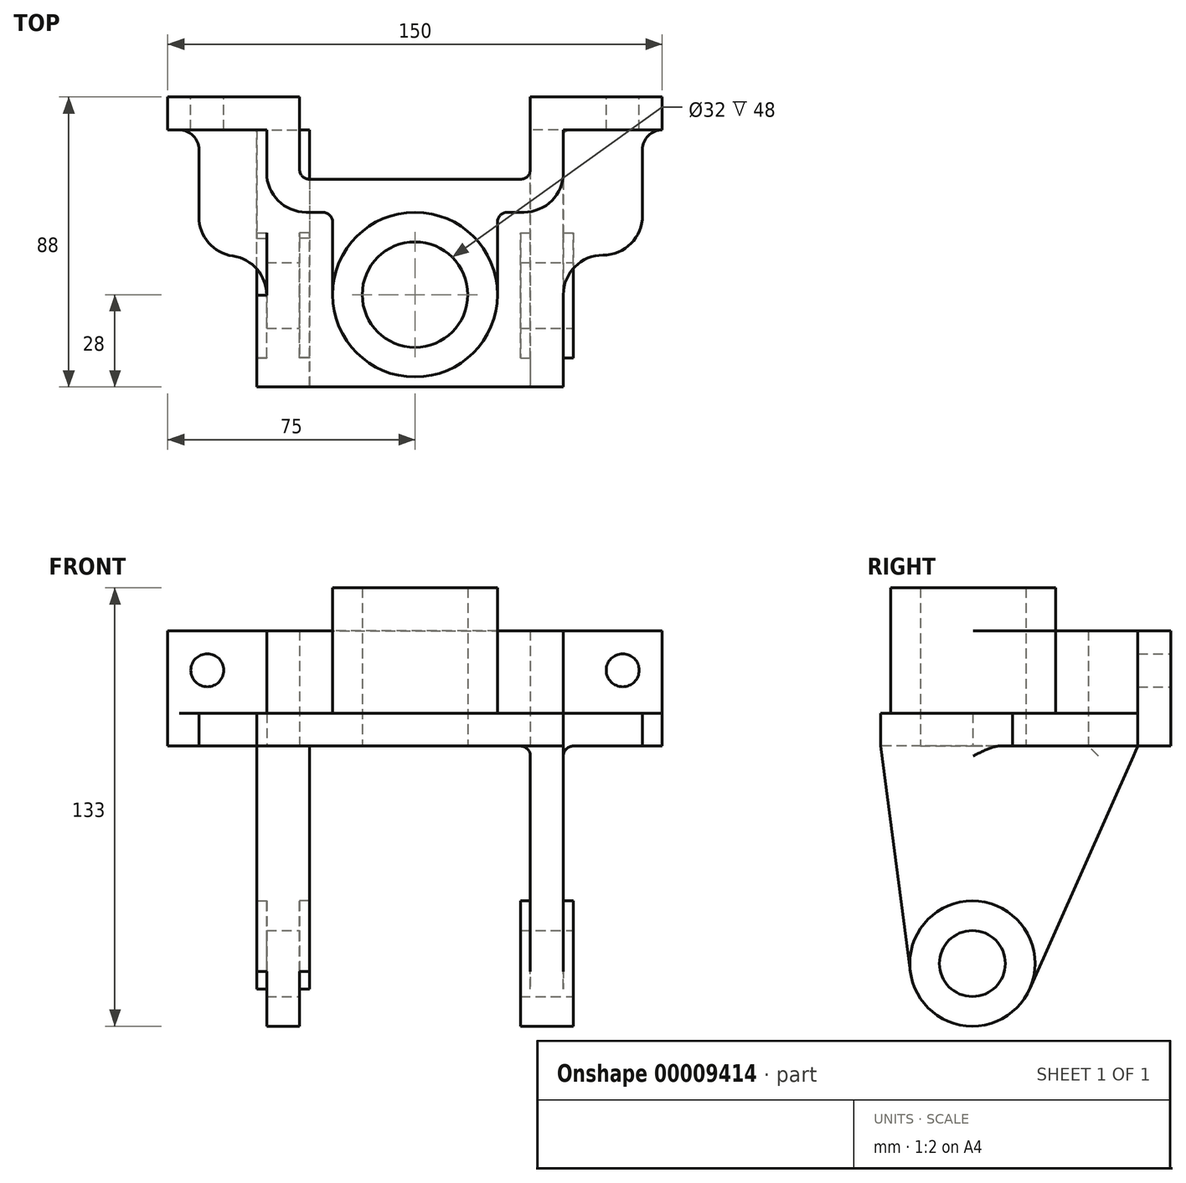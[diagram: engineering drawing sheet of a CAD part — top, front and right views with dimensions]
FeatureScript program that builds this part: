
annotation { "Feature Type Name" : "Feature", "Feature Type Description" : "" }
export const myFeature = defineFeature(function(context is Context, id is Id, definition is map)
    precondition{}
    {
        {
            var Q0;
            Q0=qCreatedBy(makeId("Top.planeOp"),FACE);
            var sketch = newSketch(context, id + "F0", { "sketchPlane" : qUnion([Q0])});
            skLineSegment(sketch, "E0", {"start": v(0, 35) * mm, "end": v(-32, 35) * mm});
            skLineSegment(sketch, "E1", {"start": v(-35, 38) * mm, "end": v(-35, 60) * mm});
            skLineSegment(sketch, "E2", {"start": v(-35, 60) * mm, "end": v(-75, 60) * mm});
            skLineSegment(sketch, "E3", {"start": v(-75, 60) * mm, "end": v(-75, 50) * mm});
            skLineSegment(sketch, "E4", {"start": v(-75, 50) * mm, "end": v(-71.53, 50) * mm});
            skLineSegment(sketch, "E5", {"start": v(-45, 50) * mm, "end": v(-45, 37) * mm});
            skLineSegment(sketch, "E6", {"start": v(-33, 25) * mm, "end": v(-28, 25) * mm});
            skLineSegment(sketch, "E7.0.MirrorCS", {"start": v(35, 38) * mm, "end": v(35, 60) * mm});
            skLineSegment(sketch, "E7.1.MirrorCS", {"start": v(0, 35) * mm, "end": v(32, 35) * mm});
            skLineSegment(sketch, "E7.2.MirrorCS", {"start": v(75, 60) * mm, "end": v(75, 50) * mm});
            skLineSegment(sketch, "E7.3.MirrorCS", {"start": v(33, 25) * mm, "end": v(28, 25) * mm});
            skLineSegment(sketch, "E7.4.MirrorCS", {"start": v(35, 60) * mm, "end": v(75, 60) * mm});
            skLineSegment(sketch, "E7.5.MirrorCS", {"start": v(75, 50) * mm, "end": v(75, 50) * mm});
            skLineSegment(sketch, "E7.6.MirrorCS", {"start": v(45, 50) * mm, "end": v(45, 37) * mm});
            skPoint(sketch, "E8.visualSharp", {"position": v(-35, 35) * mm});
            skArc(sketch, "E8.filletArc", {"start": v(-35, 38) * mm, "mid": v(-34.12, 35.88) * mm, "end": v(-32, 35) * mm});
            skPoint(sketch, "E9.visualSharp", {"position": v(35, 35) * mm});
            skArc(sketch, "E9.filletArc", {"start": v(32, 35) * mm, "mid": v(34.12, 35.88) * mm, "end": v(35, 38) * mm});
            skPoint(sketch, "E10.visualSharp", {"position": v(-45, 25) * mm});
            skArc(sketch, "E10.filletArc", {"start": v(-45, 37) * mm, "mid": v(-41.49, 28.51) * mm, "end": v(-33, 25) * mm});
            skArc(sketch, "E11.filletArc", {"start": v(33, 25) * mm, "mid": v(41.49, 28.51) * mm, "end": v(45, 37) * mm});
            skLineSegment(sketch, "E12", {"start": v(-65.53, 44) * mm, "end": v(-65.53, 23.6) * mm});
            skLineSegment(sketch, "E13", {"start": v(-45, -0.16) * mm, "end": v(-45, -28) * mm});
            skLineSegment(sketch, "E14", {"start": v(-45, -28) * mm, "end": v(45, -28) * mm});
            skLineSegment(sketch, "E15", {"start": v(45, -28) * mm, "end": v(45, 0) * mm});
            skLineSegment(sketch, "E16", {"start": v(69, 24) * mm, "end": v(69, 44) * mm});
            skPoint(sketch, "E17.newPointA", {"position": v(-45, 50) * mm});
            skArc(sketch, "E17.filletArc", {"start": v(-65.53, 44) * mm, "mid": v(-67.29, 48.24) * mm, "end": v(-71.53, 50) * mm});
            skLineSegment(sketch, "E18", {"start": v(-71.53, 50) * mm, "end": v(-45, 50) * mm});
            skPoint(sketch, "E19.newPointA", {"position": v(45, 50) * mm});
            skArc(sketch, "E19.filletArc", {"start": v(75, 50) * mm, "mid": v(70.76, 48.24) * mm, "end": v(69, 44) * mm});
            skLineSegment(sketch, "E20", {"start": v(45, 50) * mm, "end": v(75, 50) * mm});
            skPoint(sketch, "E21.visualSharp", {"position": v(-65.53, 12.1) * mm});
            skArc(sketch, "E21.filletArc", {"start": v(-65.53, 23.6) * mm, "mid": v(-62.6, 15.74) * mm, "end": v(-55.27, 11.72) * mm});
            skPoint(sketch, "E22.visualSharp", {"position": v(69, 11.84) * mm});
            skArc(sketch, "E22.filletArc", {"start": v(57, 12) * mm, "mid": v(65.49, 15.51) * mm, "end": v(69, 24) * mm});
            skCircle(sketch, "E23", {"center": v(0, 0) * mm, "radius": 25 * mm});
            skCircle(sketch, "E24", {"center": v(0, 0) * mm, "radius": 16 * mm});
            skLineSegment(sketch, "E25", {"start": v(25, 0) * mm, "end": v(25, 22) * mm});
            skLineSegment(sketch, "E26", {"start": v(-25, 0) * mm, "end": v(-25, 22) * mm});
            skPoint(sketch, "E27.orphan", {"position": v(0, 25) * mm});
            skPoint(sketch, "E28.visualSharp", {"position": v(-25, 25) * mm});
            skArc(sketch, "E28.filletArc", {"start": v(-25, 22) * mm, "mid": v(-25.88, 24.12) * mm, "end": v(-28, 25) * mm});
            skPoint(sketch, "E29.visualSharp", {"position": v(25, 25) * mm});
            skArc(sketch, "E29.filletArc", {"start": v(28, 25) * mm, "mid": v(25.88, 24.12) * mm, "end": v(25, 22) * mm});
            skPoint(sketch, "E30.visualSharp", {"position": v(45, 11.84) * mm});
            skArc(sketch, "E30.filletArc", {"start": v(57, 12) * mm, "mid": v(48.51, 8.49) * mm, "end": v(45, 0) * mm});
            skPoint(sketch, "E31.visualSharp", {"position": v(-45, 11.84) * mm});
            skArc(sketch, "E31.filletArc", {"start": v(-45, -0.16) * mm, "mid": v(-47.92, 7.7) * mm, "end": v(-55.27, 11.72) * mm});
            skLineSegment(sketch, "E32", {"start": v(-35, -0.16) * mm, "end": v(-35, -28) * mm});
            skLineSegment(sketch, "E33", {"start": v(35, 25.17) * mm, "end": v(35, -28) * mm});
            skLineSegment(sketch, "E34", {"start": v(45, 0) * mm, "end": v(45, 25) * mm});
            skLineSegment(sketch, "E35", {"start": v(-35, -0.16) * mm, "end": v(-35, 25.17) * mm});
            skLineSegment(sketch, "E36", {"start": v(-45, -0.16) * mm, "end": v(-45, 25) * mm});
            skLineSegment(sketch, "E37", {"start": v(45, 25) * mm, "end": v(45, 37) * mm});
            skLineSegment(sketch, "E38", {"start": v(-45, 25) * mm, "end": v(-45, 37) * mm});
            skLineSegment(sketch, "E39", {"start": v(45, 50) * mm, "end": v(35, 50) * mm});
            skLineSegment(sketch, "E40", {"start": v(35, 25.17) * mm, "end": v(35, 38) * mm});
            skLineSegment(sketch, "E41", {"start": v(-35, 25.17) * mm, "end": v(-35, 38) * mm});
            skLineSegment(sketch, "E42", {"start": v(-45, 50) * mm, "end": v(-35, 50) * mm});
            skSolve(sketch);
        }
        {
            var Q0;
            Q0=makeQuery(id+"F0.imprint","IMPRINT",FACE,{"disambiguationData":[TD([[makeQuery(id+"F0.imprint","IMPRINT",EDGE,{"derivedFrom":sQuery(id+"F0.wireOp",EDGE,"E24")}),-1.0]])]});
            extrude(context, id + "F1", {"entities" : qUnion([Q0]), "depth" : 48 * mm});
        }
        {
            var Q0;
            Q0=makeQuery(id+"F0.imprint","IMPRINT",FACE,{"disambiguationData":[TD([[makeQuery(id+"F0.imprint","IMPRINT",EDGE,{"derivedFrom":sQuery(id+"F0.wireOp",EDGE,"E0")}),1.0]])]});
            var Q1;
            Q1=makeQuery(id+"F0.imprint","IMPRINT",FACE,{"disambiguationData":[TD([[makeQuery(id+"F0.imprint","IMPRINT",EDGE,{"derivedFrom":sQuery(id+"F0.wireOp",EDGE,"E7.2.MirrorCS")}),-1.0]])]});
            var Q2;
            {var subQ3=sQuery(id+"F0.wireOp",EDGE,"E7.6.MirrorCS");Q2=makeQuery(id+"F0.imprint","IMPRINT",FACE,{"disambiguationData":[TD([[makeQuery(id+"F0.imprint","IMPRINT",EDGE,{"derivedFrom":subQ3}),-1.0]])]});}
            var Q3;
            {var subQ3=sQuery(id+"F0.wireOp",EDGE,"E5");Q3=makeQuery(id+"F0.imprint","IMPRINT",FACE,{"disambiguationData":[TD([[makeQuery(id+"F0.imprint","IMPRINT",EDGE,{"derivedFrom":subQ3}),1.0]])]});}
            var Q4;
            {var subQ1=sQuery(id+"F0.wireOp",EDGE,"E2");Q4=makeQuery(id+"F0.imprint","IMPRINT",FACE,{"disambiguationData":[TD([[makeQuery(id+"F0.imprint","IMPRINT",EDGE,{"derivedFrom":subQ1}),1.0]])]});}
            extrude(context, id + "F2", {"entities" : qUnion([Q0, Q1, Q2, Q3, Q4]), "operationType" : NewBodyOperationType.ADD, "depth" : 35 * mm});
        }
        {
            var Q0;
            Q0=makeQuery(id+"F0.imprint","IMPRINT",FACE,{"disambiguationData":[TD([[makeQuery(id+"F0.imprint","IMPRINT",EDGE,{"derivedFrom":sQuery(id+"F0.wireOp",EDGE,"E5")}),-1.0]])]});
            var Q1;
            {var subQ2=sQuery(id+"F0.wireOp",EDGE,"E13");Q1=makeQuery(id+"F0.imprint","IMPRINT",FACE,{"disambiguationData":[TD([[makeQuery(id+"F0.imprint","IMPRINT",EDGE,{"derivedFrom":subQ2}),1.0]])]});}
            var Q2;
            {var subQ1=sQuery(id+"F0.wireOp",EDGE,"E15");Q2=makeQuery(id+"F0.imprint","IMPRINT",FACE,{"disambiguationData":[TD([[makeQuery(id+"F0.imprint","IMPRINT",EDGE,{"derivedFrom":subQ1}),1.0]])]});}
            var Q3;
            {var subQ2=sQuery(id+"F0.wireOp",EDGE,"E7.6.MirrorCS");Q3=makeQuery(id+"F0.imprint","IMPRINT",FACE,{"disambiguationData":[TD([[makeQuery(id+"F0.imprint","IMPRINT",EDGE,{"derivedFrom":subQ2}),1.0]])]});}
            var Q4;
            {var subQ8=sQuery(id+"F0.wireOp",EDGE,"E6");Q4=makeQuery(id+"F0.imprint","IMPRINT",FACE,{"disambiguationData":[TD([[makeQuery(id+"F0.imprint","IMPRINT",EDGE,{"derivedFrom":subQ8}),-1.0]])]});}
            var Q5;
            {var subQ1=sQuery(id+"F0.wireOp",EDGE,"d0786e6e-3a46-4e64-bf30-19189b01eaf3");Q5=makeQuery(id+"F0.imprint","IMPRINT",FACE,{"disambiguationData":[TD([[makeQuery(id+"F0.imprint","IMPRINT",EDGE,{"derivedFrom":subQ1}),-1.0]])]});}
            var Q6;
            {var subQ1=sQuery(id+"F0.wireOp",EDGE,"a1b5c434-1ed9-493c-be9e-ea0c3d859ba8");Q6=makeQuery(id+"F0.imprint","IMPRINT",FACE,{"disambiguationData":[TD([[makeQuery(id+"F0.imprint","IMPRINT",EDGE,{"derivedFrom":subQ1}),1.0]])]});}
            extrude(context, id + "F3", {"entities" : qUnion([Q0, Q1, Q2, Q3, Q4, Q5, Q6]), "operationType" : NewBodyOperationType.ADD, "depth" : 10 * mm});
        }
        {
            var Q0;
            Q0=makeQuery(id+"F2.opExtrude","SWEPT_FACE",FACE,{"disambiguationData":[OSD([sQuery(id+"F0.wireOp",EDGE,"E7.4.MirrorCS")])]});
            var sketch = newSketch(context, id + "F4", { "sketchPlane" : qUnion([Q0])});
            skCircle(sketch, "E43", {"center": v(-63, 23) * mm, "radius": 5 * mm});
            skCircle(sketch, "E44", {"center": v(63, 23) * mm, "radius": 5 * mm});
            skSolve(sketch);
        }
        {
            var Q0;
            Q0=makeQuery(id+"F4.imprint","IMPRINT",FACE,{"disambiguationData":[TD([[makeQuery(id+"F4.imprint","IMPRINT",EDGE,{"derivedFrom":sQuery(id+"F4.wireOp",EDGE,"E43")}),1.0]])]});
            var Q1;
            Q1=makeQuery(id+"F4.imprint","IMPRINT",FACE,{"disambiguationData":[TD([[makeQuery(id+"F4.imprint","IMPRINT",EDGE,{"derivedFrom":sQuery(id+"F4.wireOp",EDGE,"E44")}),1.0]])]});
            var Q2;
            Q2=makeQuery(id+"F2.opExtrude","SWEPT_FACE",FACE,{"disambiguationData":[OSD([sQuery(id+"F0.wireOp",EDGE,"E4"),sQuery(id+"F0.wireOp",EDGE,"E18")])]});
            extrude(context, id + "F5", {"entities" : qUnion([Q0, Q1]), "operationType" : NewBodyOperationType.REMOVE, "endBound" : BoundingType.UP_TO_SURFACE, "oppositeDirection" : true, "endBoundEntityFace" : qUnion([Q2]), "depth" : 25 * mm});
        }
        {
            var Q0;
            {var subQ2=sQuery(id+"F0.wireOp",EDGE,"E13");Q0=makeQuery(id+"F0.imprint","IMPRINT",FACE,{"disambiguationData":[TD([[makeQuery(id+"F0.imprint","IMPRINT",EDGE,{"derivedFrom":subQ2}),1.0]])]});}
            var Q1;
            {var subQ1=sQuery(id+"F0.wireOp",EDGE,"E15");Q1=makeQuery(id+"F0.imprint","IMPRINT",FACE,{"disambiguationData":[TD([[makeQuery(id+"F0.imprint","IMPRINT",EDGE,{"derivedFrom":subQ1}),1.0]])]});}
            var Q2;
            {var subQ3=sQuery(id+"F0.wireOp",EDGE,"E5");Q2=makeQuery(id+"F0.imprint","IMPRINT",FACE,{"disambiguationData":[TD([[makeQuery(id+"F0.imprint","IMPRINT",EDGE,{"derivedFrom":subQ3}),1.0]])]});}
            var Q3;
            {var subQ3=sQuery(id+"F0.wireOp",EDGE,"E7.6.MirrorCS");Q3=makeQuery(id+"F0.imprint","IMPRINT",FACE,{"disambiguationData":[TD([[makeQuery(id+"F0.imprint","IMPRINT",EDGE,{"derivedFrom":subQ3}),-1.0]])]});}
            extrude(context, id + "F6", {"entities" : qUnion([Q0, Q1, Q2, Q3]), "operationType" : NewBodyOperationType.ADD, "oppositeDirection" : true, "depth" : 100 * mm});
        }
        {
            var Q0;
            {var subQ0=sQuery(id+"F0.wireOp",EDGE,"E15");Q0=makeQuery(id+"F6.boolean.opBoolean","MERGE",FACE,{"derivedFrom":[makeQuery(id+"F3.opExtrude","SWEPT_FACE",FACE,{"disambiguationData":[OSD([subQ0])]}),makeQuery(id+"F6.opExtrude","SWEPT_FACE",FACE,{"disambiguationData":[OSD([subQ0,sQuery(id+"F0.wireOp",EDGE,"E34")])]})]});}
            var sketch = newSketch(context, id + "F7", { "sketchPlane" : qUnion([Q0])});
            skCircle(sketch, "E45", {"center": v(-0.22, -66) * mm, "radius": 10 * mm});
            skArc(sketch, "E46", {"start": v(-19.06, -68.46) * mm, "mid": v(-2.95, -84.8) * mm, "end": v(17.14, -73.73) * mm});
            skLineSegment(sketch, "E47", {"start": v(-28, 0) * mm, "end": v(-19.06, -68.46) * mm});
            skLineSegment(sketch, "E48", {"start": v(-28, 0) * mm, "end": v(50, 0) * mm});
            skLineSegment(sketch, "E49", {"start": v(50, 0) * mm, "end": v(17.14, -73.73) * mm});
            skLineSegment(sketch, "E50", {"start": v(50, 0) * mm, "end": v(-28, 0) * mm});
            skArc(sketch, "E51", {"start": v(17.14, -73.73) * mm, "mid": v(2.52, -47.2) * mm, "end": v(-19.06, -68.46) * mm});
            skSolve(sketch);
        }
        {
            var Q0;
            Q0=makeQuery(id+"F7.imprint","IMPRINT",FACE,{"disambiguationData":[TD([[makeQuery(id+"F7.imprint","IMPRINT",EDGE,{"derivedFrom":sQuery(id+"F7.wireOp",EDGE,"E46")}),-1.0]])]});
            var Q1;
            Q1=makeQuery(id+"F7.imprint","IMPRINT",FACE,{"disambiguationData":[TD([[makeQuery(id+"F7.imprint","IMPRINT",EDGE,{"derivedFrom":sQuery(id+"F7.wireOp",EDGE,"E45")}),1.0]])]});
            extrude(context, id + "F8", {"entities" : qUnion([Q0, Q1]), "operationType" : NewBodyOperationType.REMOVE, "endBound" : BoundingType.THROUGH_ALL, "oppositeDirection" : true, "depth" : 25 * mm});
        }
        {
            var Q0;
            Q0=makeQuery(id+"F7.imprint","IMPRINT",FACE,{"disambiguationData":[TD([[makeQuery(id+"F7.imprint","IMPRINT",EDGE,{"derivedFrom":sQuery(id+"F7.wireOp",EDGE,"E45")}),-1.0]])]});
            extrude(context, id + "F9", {"entities" : qUnion([Q0]), "operationType" : NewBodyOperationType.ADD, "depth" : 3 * mm});
        }
        {
            var Q0;
            Q0=makeQuery(id+"F9.opExtrude","CAP_FACE",FACE,{"disambiguationData":[OSD([sQuery(id+"F7.wireOp",EDGE,"E45"),sQuery(id+"F7.wireOp",EDGE,"E46"),sQuery(id+"F7.wireOp",EDGE,"E51")])],"isStart":false});
            extrude(context, id + "F10", {"entities" : qUnion([Q0]), "operationType" : NewBodyOperationType.ADD, "oppositeDirection" : true, "depth" : 16 * mm});
        }
        {
            var Q0;
            {var subQ0=sQuery(id+"F0.wireOp",EDGE,"E13");Q0=makeQuery(id+"F6.boolean.opBoolean","MERGE",FACE,{"derivedFrom":[makeQuery(id+"F3.opExtrude","SWEPT_FACE",FACE,{"disambiguationData":[OSD([subQ0])]}),makeQuery(id+"F6.opExtrude","SWEPT_FACE",FACE,{"disambiguationData":[OSD([sQuery(id+"F0.wireOp",EDGE,"E5"),subQ0,sQuery(id+"F0.wireOp",EDGE,"E36"),sQuery(id+"F0.wireOp",EDGE,"E38")])]})]});}
            var sketch = newSketch(context, id + "F11", { "sketchPlane" : qUnion([Q0])});
            skCircle(sketch, "E52", {"center": v(0.22, -66) * mm, "radius": 19 * mm});
            skSolve(sketch);
        }
        {
            var Q0;
            {var subQ1=sQuery(id+"F11.wireOp",EDGE,"E52");Q0=makeQuery(id+"F11.imprint","IMPRINT",FACE,{"disambiguationData":[TD([[makeQuery(id+"F11.imprint","IMPRINT",EDGE,{"disambiguationData":[OD(0.0)],"derivedFrom":subQ1}),-1.0]])]});}
            extrude(context, id + "F12", {"entities" : qUnion([Q0]), "operationType" : NewBodyOperationType.ADD, "depth" : 3 * mm});
        }
        {
            var Q0;
            Q0=makeQuery(id+"F12.opExtrude","CAP_FACE",FACE,{"disambiguationData":[OSD([sQuery(id+"F0.wireOp",EDGE,"E5"),sQuery(id+"F0.wireOp",EDGE,"E13"),sQuery(id+"F0.wireOp",EDGE,"E36"),sQuery(id+"F0.wireOp",EDGE,"E38"),sQuery(id+"F7.wireOp",EDGE,"E45"),sQuery(id+"F11.wireOp",EDGE,"E52")])],"isStart":false});
            extrude(context, id + "F13", {"entities" : qUnion([Q0]), "operationType" : NewBodyOperationType.ADD, "oppositeDirection" : true, "depth" : 16 * mm});
        }
        {
            var Q0;
            Q0=makeQuery(id+"F3.opExtrude","CAP_EDGE",EDGE,{"disambiguationData":[OSD([sQuery(id+"F0.wireOp",EDGE,"E11.filletArc")])],"isStart":false});
            var Q1;
            Q1=makeQuery(id+"F3.opExtrude","CAP_EDGE",EDGE,{"disambiguationData":[OSD([sQuery(id+"F0.wireOp",EDGE,"E20")])],"isStart":false});
            var Q2;
            Q2=makeQuery(id+"F3.opExtrude","CAP_EDGE",EDGE,{"disambiguationData":[OSD([sQuery(id+"F0.wireOp",EDGE,"E18")])],"isStart":false});
            var Q3;
            Q3=makeQuery(id+"F6.opExtrude","CAP_EDGE",EDGE,{"disambiguationData":[OSD([sQuery(id+"F0.wireOp",EDGE,"E1"),sQuery(id+"F0.wireOp",EDGE,"E32"),sQuery(id+"F0.wireOp",EDGE,"E35"),sQuery(id+"F0.wireOp",EDGE,"E41")])],"isStart":true});
            var Q4;
            Q4=makeQuery(id+"F6.opExtrude","CAP_EDGE",EDGE,{"disambiguationData":[OSD([sQuery(id+"F0.wireOp",EDGE,"E7.0.MirrorCS"),sQuery(id+"F0.wireOp",EDGE,"E33"),sQuery(id+"F0.wireOp",EDGE,"E40")])],"isStart":true});
            var Q5;
            Q5=makeQuery(id+"F6.opExtrude","CAP_EDGE",EDGE,{"disambiguationData":[OSD([sQuery(id+"F0.wireOp",EDGE,"E5"),sQuery(id+"F0.wireOp",EDGE,"E13"),sQuery(id+"F0.wireOp",EDGE,"E36"),sQuery(id+"F0.wireOp",EDGE,"E38")])],"isStart":true});
            var Q6;
            Q6=makeQuery(id+"F6.opExtrude","CAP_EDGE",EDGE,{"disambiguationData":[OSD([sQuery(id+"F0.wireOp",EDGE,"E7.6.MirrorCS"),sQuery(id+"F0.wireOp",EDGE,"E15"),sQuery(id+"F0.wireOp",EDGE,"E34"),sQuery(id+"F0.wireOp",EDGE,"E37")])],"isStart":true});
            var Q7;
            Q7=makeQuery(id+"F2.opExtrude","CAP_EDGE",EDGE,{"disambiguationData":[OSD([sQuery(id+"F0.wireOp",EDGE,"E23")])],"isStart":false});
            fillet(context, id + "F14", {"entities" : qUnion([Q0, Q1, Q2, Q3, Q4, Q5, Q6, Q7]), "radius" : 3 * mm, "tangentPropagation" : true, "allowEdgeOverflow" : false});
        }
    });
